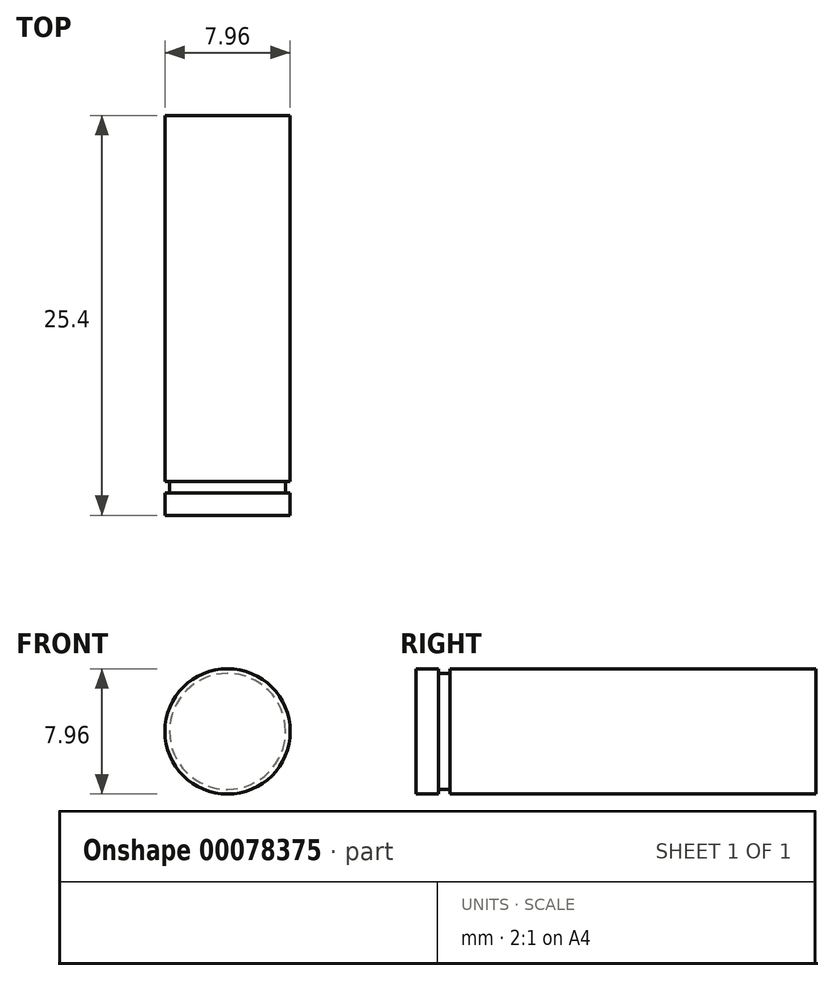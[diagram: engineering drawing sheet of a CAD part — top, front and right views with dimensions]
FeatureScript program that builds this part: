
annotation { "Feature Type Name" : "Feature", "Feature Type Description" : "" }
export const myFeature = defineFeature(function(context is Context, id is Id, definition is map)
    precondition{}
    {
        {
            var Q0;
            Q0=qCreatedBy(makeId("Front.planeOp"),FACE);
            var sketch = newSketch(context, id + "F0", { "sketchPlane" : qUnion([Q0])});
            skCircle(sketch, "E0", {"center": v(0, 0) * mm, "radius": 3.98 * mm});
            skSolve(sketch);
        }
        {
            var Q0;
            Q0 = qSketchRegion(id + "F0", true);
            extrude(context, id + "F1", {"entities" : qUnion([Q0]), "depth" : 25.4 * mm});
        }
        {
            var Q0;
            Q0=qCreatedBy(makeId("Front.planeOp"),FACE);
            cPlane(context, id + "F2", {"entities" : qUnion([Q0]), "cplaneType" : CPlaneType.OFFSET, "offset" : 23.24 * mm, "width" : 152.4 * mm, "height" : 152.4 * mm});
        }
        {
            var Q0;
            Q0=qCreatedBy(id+"F2.planeOp",FACE);
            var sketch = newSketch(context, id + "F3", { "sketchPlane" : qUnion([Q0])});
            skCircle(sketch, "E1", {"center": v(0, 0) * mm, "radius": 3.68 * mm});
            skCircle(sketch, "E2", {"center": v(0, 0) * mm, "radius": 7.39 * mm});
            skSolve(sketch);
        }
        {
            var Q0;
            Q0=makeQuery(id+"F3.imprint","IMPRINT",FACE,{"disambiguationData":[TD([[makeQuery(id+"F3.imprint","IMPRINT",EDGE,{"derivedFrom":sQuery(id+"F3.wireOp",EDGE,"E1")}),-1.0]])]});
            extrude(context, id + "F4", {"entities" : qUnion([Q0]), "operationType" : NewBodyOperationType.REMOVE, "depth" : 0.74 * mm});
        }
    });
